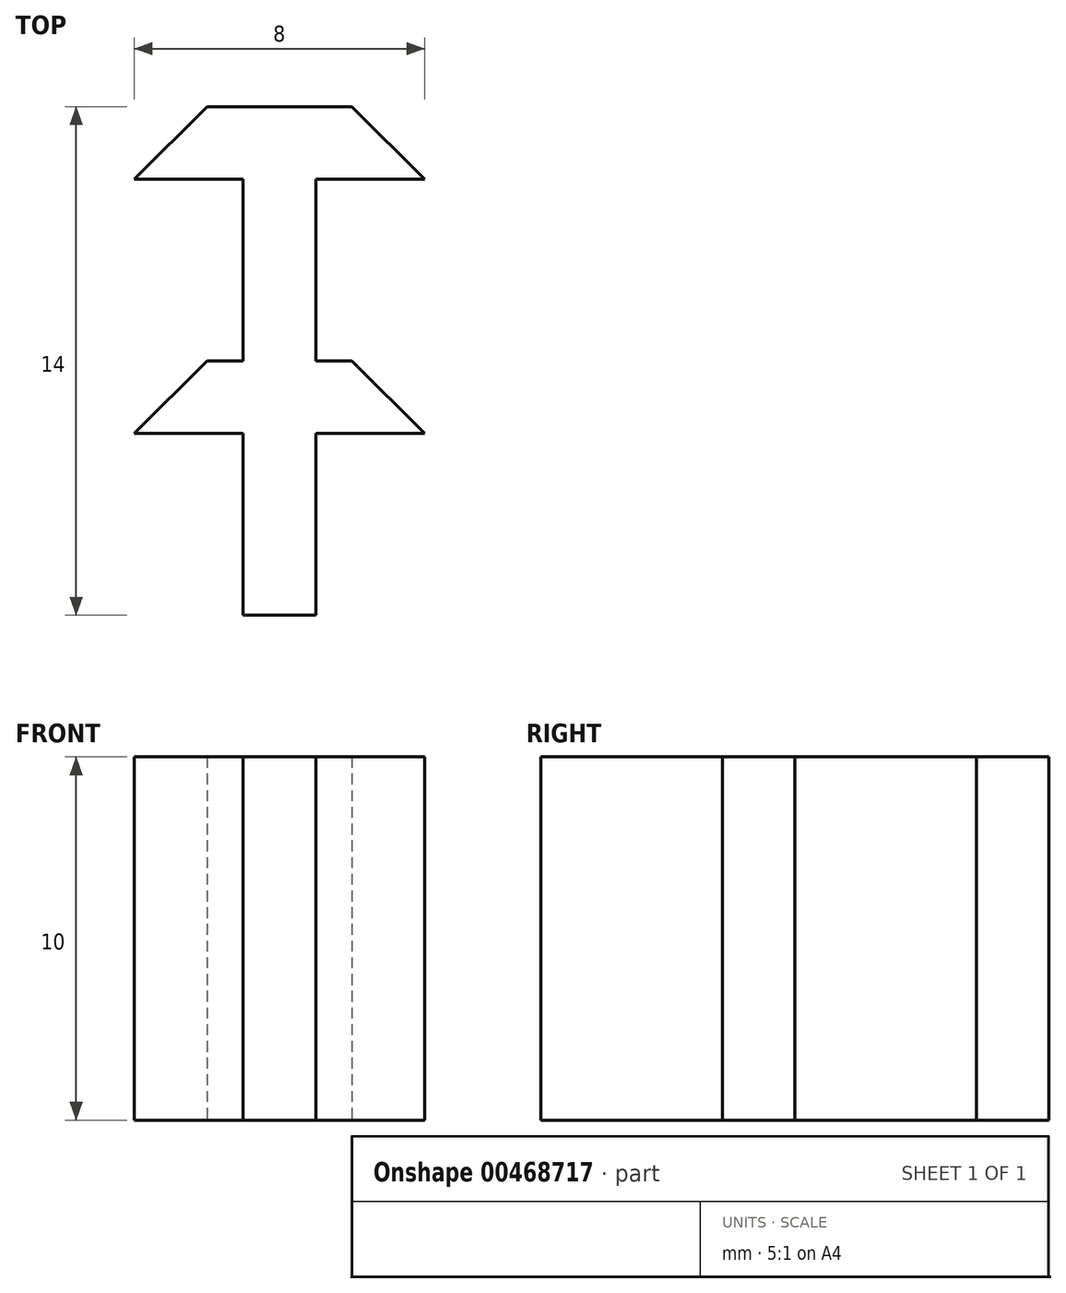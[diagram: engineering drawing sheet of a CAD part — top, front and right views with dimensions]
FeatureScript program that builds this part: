
annotation { "Feature Type Name" : "Feature", "Feature Type Description" : "" }
export const myFeature = defineFeature(function(context is Context, id is Id, definition is map)
    precondition{}
    {
        {
            var Q0;
            Q0=qCreatedBy(makeId("Top.planeOp"),FACE);
            var sketch = newSketch(context, id + "F0", { "sketchPlane" : qUnion([Q0])});
            skLineSegment(sketch, "E0", {"start": v(0, 8.46) * mm, "end": v(-2, 8.46) * mm});
            skLineSegment(sketch, "E1", {"start": v(-2, 8.46) * mm, "end": v(-4, 6.46) * mm});
            skLineSegment(sketch, "E2", {"start": v(-4, 6.46) * mm, "end": v(-1, 6.46) * mm});
            skLineSegment(sketch, "E3", {"start": v(-1, 6.46) * mm, "end": v(-1, 1.46) * mm});
            skLineSegment(sketch, "E4", {"start": v(-1, 1.46) * mm, "end": v(-1, 1.46) * mm});
            skLineSegment(sketch, "E5", {"start": v(-4, -0.54) * mm, "end": v(-1, -0.54) * mm});
            skLineSegment(sketch, "E6", {"start": v(-1, -0.54) * mm, "end": v(-1, -5.54) * mm});
            skLineSegment(sketch, "E7", {"start": v(-1, -5.54) * mm, "end": v(0, -5.54) * mm});
            skLineSegment(sketch, "E8", {"start": v(0, -5.54) * mm, "end": v(0, 8.46) * mm});
            skLineSegment(sketch, "E9", {"start": v(-4, -0.54) * mm, "end": v(-2, 1.46) * mm});
            skLineSegment(sketch, "E10", {"start": v(-2, 1.46) * mm, "end": v(-1, 1.46) * mm});
            skLineSegment(sketch, "E11.MirrorCS", {"start": v(1, -5.54) * mm, "end": v(0, -5.54) * mm});
            skLineSegment(sketch, "E12.MirrorCS", {"start": v(4, -0.54) * mm, "end": v(1, -0.54) * mm});
            skLineSegment(sketch, "E13.MirrorCS", {"start": v(2, 1.46) * mm, "end": v(1, 1.46) * mm});
            skLineSegment(sketch, "E14.MirrorCS", {"start": v(0, 8.46) * mm, "end": v(2, 8.46) * mm});
            skLineSegment(sketch, "E15.MirrorCS", {"start": v(2, 8.46) * mm, "end": v(4, 6.46) * mm});
            skLineSegment(sketch, "E16.MirrorCS", {"start": v(1, 6.46) * mm, "end": v(1, 1.46) * mm});
            skLineSegment(sketch, "E17.MirrorCS", {"start": v(4, -0.54) * mm, "end": v(2, 1.46) * mm});
            skLineSegment(sketch, "E18.MirrorCS", {"start": v(1, 1.46) * mm, "end": v(1, 1.46) * mm});
            skLineSegment(sketch, "E19.MirrorCS", {"start": v(4, 6.46) * mm, "end": v(1, 6.46) * mm});
            skLineSegment(sketch, "E20.MirrorCS", {"start": v(1, -0.54) * mm, "end": v(1, -5.54) * mm});
            skSolve(sketch);
        }
        {
            var Q0;
            Q0 = qSketchRegion(id + "F0", true);
            extrude(context, id + "F1", {"entities" : qUnion([Q0]), "depth" : 10 * mm});
        }
    });
